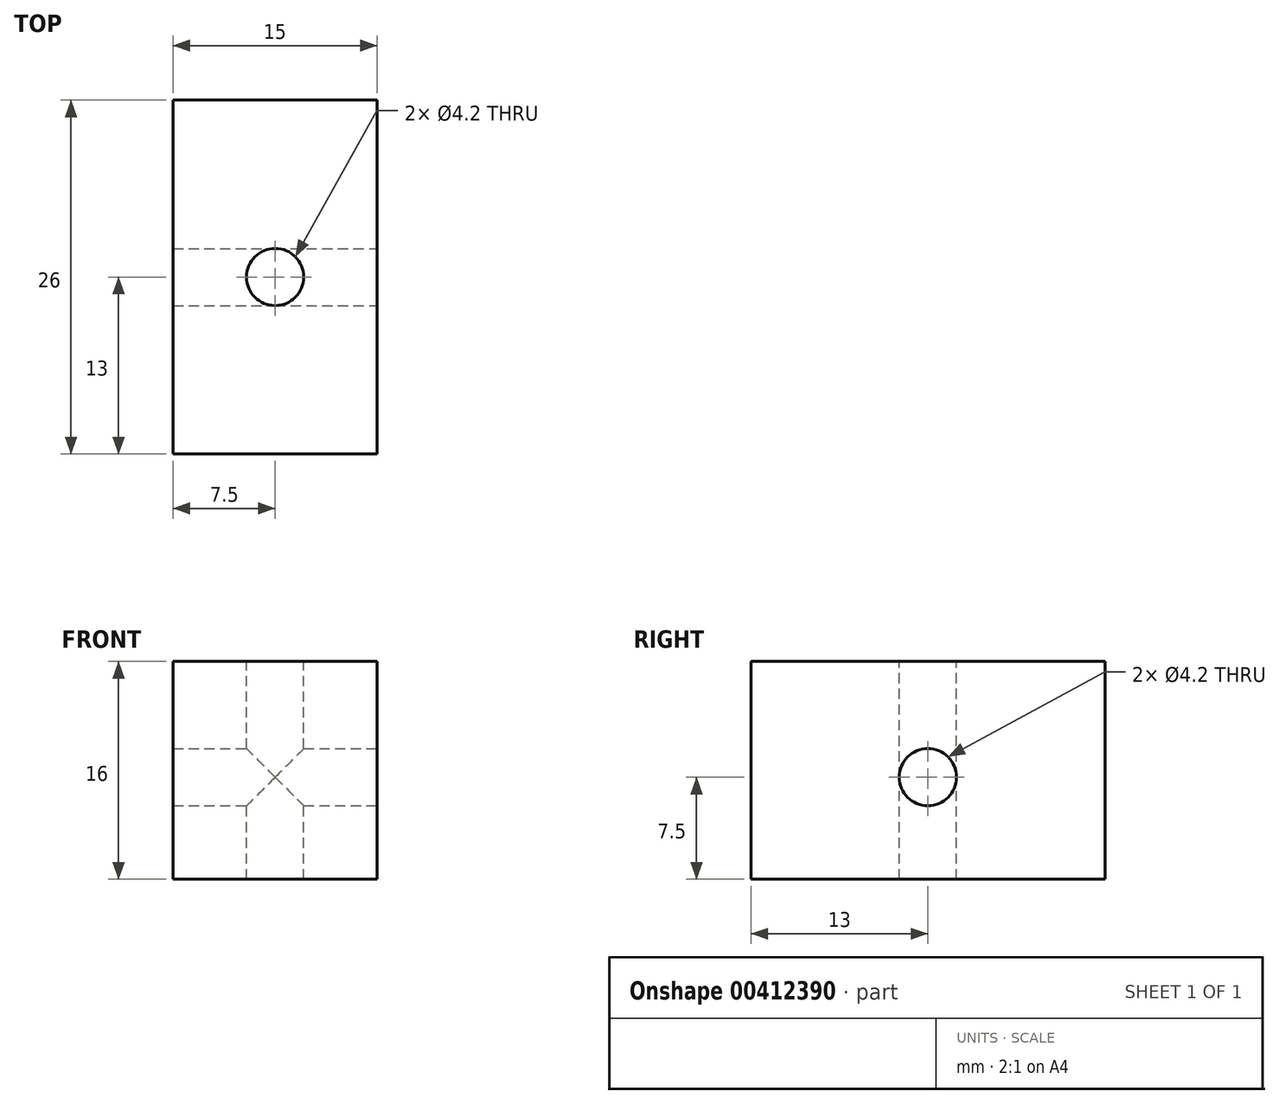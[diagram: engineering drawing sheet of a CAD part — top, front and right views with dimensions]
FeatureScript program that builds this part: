
annotation { "Feature Type Name" : "Feature", "Feature Type Description" : "" }
export const myFeature = defineFeature(function(context is Context, id is Id, definition is map)
    precondition{}
    {
        {
            var Q0;
            Q0=qCreatedBy(makeId("Top.planeOp"),FACE);
            var sketch = newSketch(context, id + "F0", { "sketchPlane" : qUnion([Q0])});
            skLineSegment(sketch, "E0.bottom", {"start": v(0, 0) * mm, "end": v(15, 0) * mm});
            skLineSegment(sketch, "E0.top", {"start": v(0, 26) * mm, "end": v(15, 26) * mm});
            skLineSegment(sketch, "E0.left", {"start": v(0, 0) * mm, "end": v(0, 26) * mm});
            skLineSegment(sketch, "E0.right", {"start": v(15, 0) * mm, "end": v(15, 26) * mm});
            skSolve(sketch);
        }
        {
            var Q0;
            Q0 = qSketchRegion(id + "F0", true);
            extrude(context, id + "F1", {"entities" : qUnion([Q0]), "depth" : 16 * mm});
        }
        {
            var Q0;
            Q0=makeQuery(id+"F1.opExtrude","CAP_FACE",FACE,{"disambiguationData":[OSD([sQuery(id+"F0.wireOp",EDGE,"E0.bottom"),sQuery(id+"F0.wireOp",EDGE,"E0.top"),sQuery(id+"F0.wireOp",EDGE,"E0.left"),sQuery(id+"F0.wireOp",EDGE,"E0.right")])],"isStart":false});
            var sketch = newSketch(context, id + "F2", { "sketchPlane" : qUnion([Q0])});
            skPoint(sketch, "E1", {"position": v(7.5, 13) * mm});
            skSolve(sketch);
        }
        {
            var Q0;
            Q0=sQuery(id+"F2.wireOp",VERTEX,"E1");
            var Q1;
            Q1=makeQuery(id+"F1.opExtrude","SWEPT_BODY",BODY,{"disambiguationData":[OSD([sQuery(id+"F0.wireOp",EDGE,"E0.bottom"),sQuery(id+"F0.wireOp",EDGE,"E0.top"),sQuery(id+"F0.wireOp",EDGE,"E0.left"),sQuery(id+"F0.wireOp",EDGE,"E0.right")])]});
            hole(context, id + "F3", {"style" : HoleStyle.SIMPLE, "endStyle" : HoleEndStyle.THROUGH, "standardTappedOrClearance" : lookupTablePath({ "standard" : "ISO", "engagement" : "75%", "pitch" : "0.8 mm", "size" : "M5", "type" : "Tapped" }), "standardBlindInLast" : lookupTablePath({ "standard" : "ISO", "engagement" : "75%", "pitch" : "0.8 mm", "size" : "M5", "type" : "Tapped" }), "holeDiameter" : 4.2 * mm, "showTappedDepth" : true, "isTappedThrough" : true, "tappedDepth" : 5 * mm, "tapClearance" : 3, "locations" : qUnion([Q0]), "scope" : qUnion([Q1]), "majorDiameter" : 5 * mm});
        }
        {
            var Q0;
            Q0=makeQuery(id+"F1.opExtrude","SWEPT_FACE",FACE,{"disambiguationData":[OSD([sQuery(id+"F0.wireOp",EDGE,"E0.right")])]});
            var sketch = newSketch(context, id + "F4", { "sketchPlane" : qUnion([Q0])});
            skPoint(sketch, "E2", {"position": v(13, 7.5) * mm});
            skSolve(sketch);
        }
        {
            var Q0;
            Q0=sQuery(id+"F4.wireOp",VERTEX,"E2");
            var Q1;
            Q1=makeQuery(id+"F1.opExtrude","SWEPT_BODY",BODY,{"disambiguationData":[OSD([sQuery(id+"F0.wireOp",EDGE,"E0.bottom"),sQuery(id+"F0.wireOp",EDGE,"E0.top"),sQuery(id+"F0.wireOp",EDGE,"E0.left"),sQuery(id+"F0.wireOp",EDGE,"E0.right")])]});
            hole(context, id + "F5", {"style" : HoleStyle.SIMPLE, "endStyle" : HoleEndStyle.THROUGH, "standardTappedOrClearance" : lookupTablePath({ "standard" : "ISO", "engagement" : "75%", "pitch" : "0.8 mm", "size" : "M5", "type" : "Tapped" }), "standardBlindInLast" : lookupTablePath({ "standard" : "ISO", "engagement" : "75%", "pitch" : "0.8 mm", "size" : "M5", "type" : "Tapped" }), "holeDiameter" : 4.2 * mm, "showTappedDepth" : true, "isTappedThrough" : true, "tappedDepth" : 5 * mm, "tapClearance" : 3, "locations" : qUnion([Q0]), "scope" : qUnion([Q1]), "majorDiameter" : 5 * mm});
        }
    });
